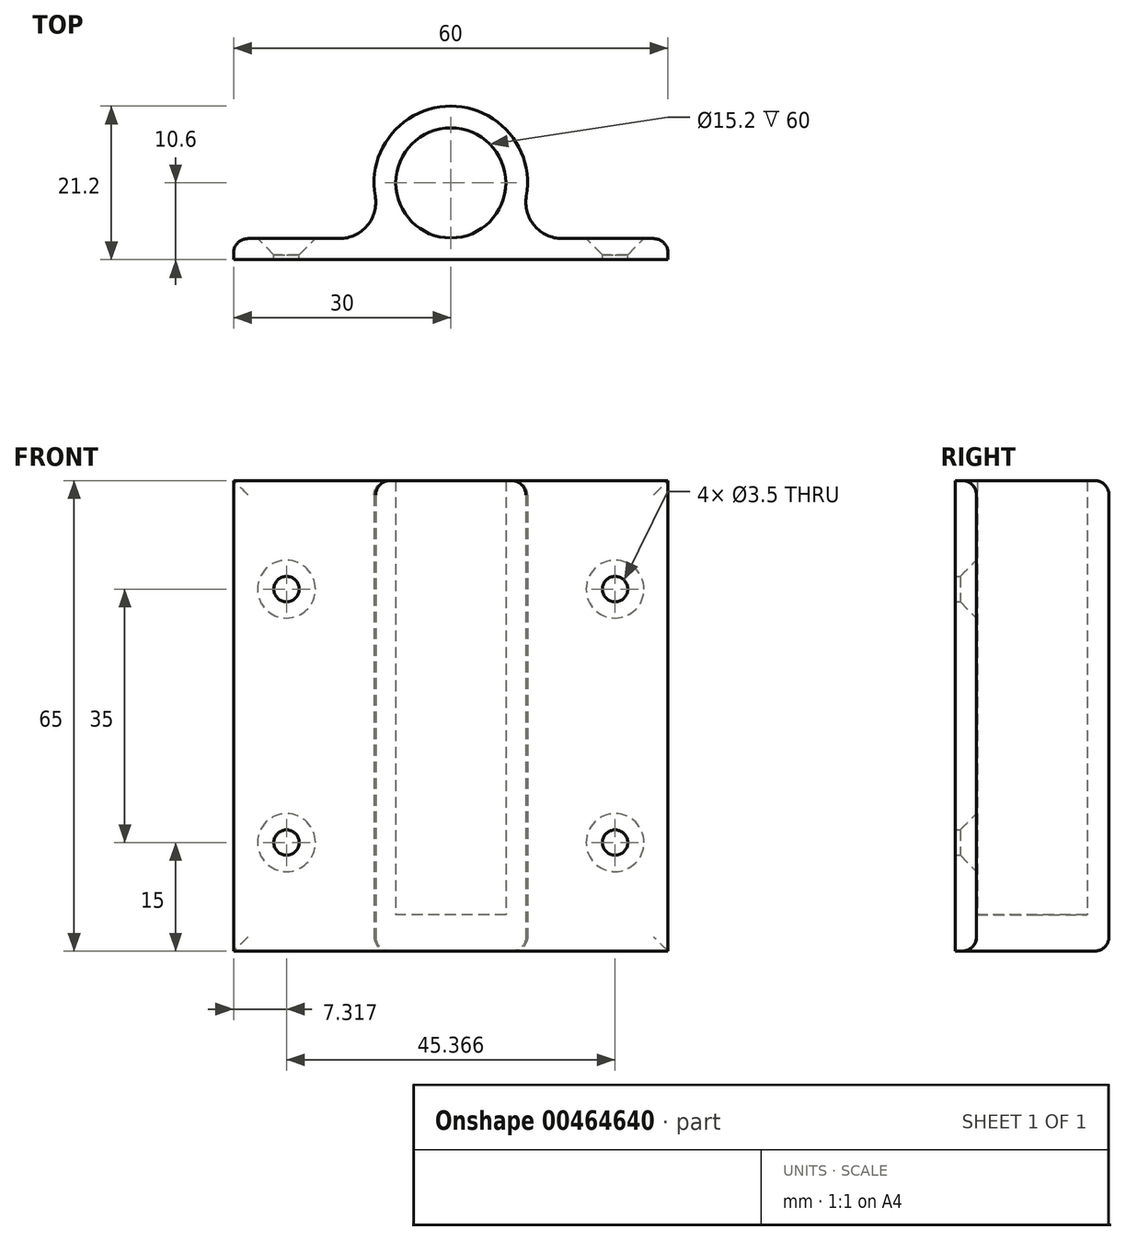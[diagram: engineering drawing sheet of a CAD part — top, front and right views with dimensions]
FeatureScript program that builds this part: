
annotation { "Feature Type Name" : "Feature", "Feature Type Description" : "" }
export const myFeature = defineFeature(function(context is Context, id is Id, definition is map)
    precondition{}
    {
        {
            var Q0;
            Q0=qCreatedBy(makeId("Top.planeOp"),FACE);
            var sketch = newSketch(context, id + "F0", { "sketchPlane" : qUnion([Q0])});
            skCircle(sketch, "E0", {"center": v(0, 0) * mm, "radius": 7.6 * mm});
            skArc(sketch, "E1.0", {"start": v(7.3, -7.7) * mm, "mid": v(0, 10.6) * mm, "end": v(-7.3, -7.7) * mm});
            skLineSegment(sketch, "E2.bottom", {"start": v(0, -10.6) * mm, "end": v(-30, -10.6) * mm});
            skLineSegment(sketch, "E2.top", {"start": v(-7.3, -7.7) * mm, "end": v(-30, -7.7) * mm});
            skLineSegment(sketch, "E2.right", {"start": v(-30, -10.6) * mm, "end": v(-30, -7.7) * mm});
            skLineSegment(sketch, "E3.bottom", {"start": v(0, -10.6) * mm, "end": v(30, -10.6) * mm});
            skLineSegment(sketch, "E3.top", {"start": v(7.3, -7.7) * mm, "end": v(30, -7.7) * mm});
            skLineSegment(sketch, "E3.right", {"start": v(30, -10.6) * mm, "end": v(30, -7.7) * mm});
            skSolve(sketch);
        }
        {
            var Q0;
            Q0=makeQuery(id+"F0.imprint","IMPRINT",FACE,{"disambiguationData":[TD([[makeQuery(id+"F0.imprint","IMPRINT",EDGE,{"derivedFrom":sQuery(id+"F0.wireOp",EDGE,"E0")}),-1.0]])]});
            var Q1;
            Q1=makeQuery(id+"F0.imprint","IMPRINT",FACE,{"disambiguationData":[TD([[makeQuery(id+"F0.imprint","IMPRINT",EDGE,{"derivedFrom":sQuery(id+"F0.wireOp",EDGE,"E0")}),1.0]])]});
            extrude(context, id + "F1", {"entities" : qUnion([Q0, Q1]), "depth" : 5 * mm});
        }
        {
            var Q0;
            Q0=makeQuery(id+"F1.opExtrude","CAP_FACE",FACE,{"disambiguationData":[OSD([sQuery(id+"F0.wireOp",EDGE,"E1.0"),sQuery(id+"F0.wireOp",EDGE,"E2.bottom"),sQuery(id+"F0.wireOp",EDGE,"E2.top"),sQuery(id+"F0.wireOp",EDGE,"E2.right"),sQuery(id+"F0.wireOp",EDGE,"E3.bottom"),sQuery(id+"F0.wireOp",EDGE,"E3.top"),sQuery(id+"F0.wireOp",EDGE,"E3.right")])],"isStart":false});
            var sketch = newSketch(context, id + "F2", { "sketchPlane" : qUnion([Q0])});
            skArc(sketch, "E4.0", {"start": v(7.3, -7.7) * mm, "mid": v(0, 10.6) * mm, "end": v(-7.3, -7.7) * mm});
            skLineSegment(sketch, "E4.1", {"start": v(7.3, -7.7) * mm, "end": v(30, -7.7) * mm});
            skLineSegment(sketch, "E4.2", {"start": v(30, -10.6) * mm, "end": v(30, -7.7) * mm});
            skLineSegment(sketch, "E4.3", {"start": v(30, -10.6) * mm, "end": v(-30, -10.6) * mm});
            skLineSegment(sketch, "E4.4", {"start": v(-30, -10.6) * mm, "end": v(-30, -7.7) * mm});
            skLineSegment(sketch, "E4.5", {"start": v(-7.3, -7.7) * mm, "end": v(-30, -7.7) * mm});
            skCircle(sketch, "E4.6", {"center": v(0, 0) * mm, "radius": 7.6 * mm});
            skSolve(sketch);
        }
        {
            var Q0;
            Q0=makeQuery(id+"F2.imprint","IMPRINT",FACE,{"disambiguationData":[TD([[makeQuery(id+"F2.imprint","IMPRINT",EDGE,{"derivedFrom":sQuery(id+"F2.wireOp",EDGE,"E4.0")}),1.0]])]});
            extrude(context, id + "F3", {"entities" : qUnion([Q0]), "operationType" : NewBodyOperationType.ADD, "depth" : 60 * mm});
        }
        {
            var Q0;
            Q0=makeQuery(id+"F3.boolean.opBoolean","MERGE",EDGE,{"derivedFrom":[makeQuery(id+"F1.opExtrude","SWEPT_EDGE",EDGE,{"disambiguationData":[OSD([sQuery(id+"F0.wireOp",EDGE,"E1.0"),sQuery(id+"F0.wireOp",EDGE,"E2.top")])]}),makeQuery(id+"F3.opExtrude","SWEPT_EDGE",EDGE,{"disambiguationData":[OSD([sQuery(id+"F2.wireOp",EDGE,"E4.0"),sQuery(id+"F2.wireOp",EDGE,"E4.5")])]})]});
            var Q1;
            Q1=makeQuery(id+"F3.boolean.opBoolean","MERGE",EDGE,{"derivedFrom":[makeQuery(id+"F1.opExtrude","SWEPT_EDGE",EDGE,{"disambiguationData":[OSD([sQuery(id+"F0.wireOp",EDGE,"E1.0"),sQuery(id+"F0.wireOp",EDGE,"E3.top")])]}),makeQuery(id+"F3.opExtrude","SWEPT_EDGE",EDGE,{"disambiguationData":[OSD([sQuery(id+"F2.wireOp",EDGE,"E4.0"),sQuery(id+"F2.wireOp",EDGE,"E4.1")])]})]});
            fillet(context, id + "F4", {"entities" : qUnion([Q0, Q1]), "radius" : 5 * mm, "tangentPropagation" : true, "allowEdgeOverflow" : false});
        }
        {
            var Q0;
            Q0=makeQuery(id+"F3.boolean.opBoolean","MERGE",FACE,{"derivedFrom":[makeQuery(id+"F1.opExtrude","SWEPT_FACE",FACE,{"disambiguationData":[OSD([sQuery(id+"F0.wireOp",EDGE,"E3.top")])]}),makeQuery(id+"F3.opExtrude","SWEPT_FACE",FACE,{"disambiguationData":[OSD([sQuery(id+"F2.wireOp",EDGE,"E4.1")])]})]});
            var sketch = newSketch(context, id + "F5", { "sketchPlane" : qUnion([Q0])});
            skLineSegment(sketch, "E5", {"start": v(-22.68, 65) * mm, "end": v(-22.68, 0) * mm, "construction": true});
            skLineSegment(sketch, "E6", {"start": v(-30, 50) * mm, "end": v(-15.37, 50) * mm, "construction": true});
            skLineSegment(sketch, "E7", {"start": v(-30, 15) * mm, "end": v(-15.37, 15) * mm, "construction": true});
            skPoint(sketch, "E8", {"position": v(-22.68, 50) * mm});
            skPoint(sketch, "E9", {"position": v(-22.68, 15) * mm});
            skLineSegment(sketch, "E10", {"start": v(0, 63) * mm, "end": v(0, 0) * mm, "construction": true});
            skPoint(sketch, "E11.MirrorP", {"position": v(22.68, 15) * mm});
            skPoint(sketch, "E12.MirrorP", {"position": v(22.68, 50) * mm});
            skSolve(sketch);
        }
        {
            var Q0;
            Q0=sQuery(id+"F5.wireOp",VERTEX,"E8");
            var Q1;
            Q1=sQuery(id+"F5.wireOp",VERTEX,"E9");
            var Q2;
            Q2=sQuery(id+"F5.wireOp",VERTEX,"E12.MirrorP");
            var Q3;
            Q3=sQuery(id+"F5.wireOp",VERTEX,"E11.MirrorP");
            var Q4;
            Q4=makeQuery(id+"F1.opExtrude","SWEPT_BODY",BODY,{"disambiguationData":[OSD([sQuery(id+"F0.wireOp",EDGE,"E1.0"),sQuery(id+"F0.wireOp",EDGE,"E2.bottom"),sQuery(id+"F0.wireOp",EDGE,"E2.top"),sQuery(id+"F0.wireOp",EDGE,"E2.right"),sQuery(id+"F0.wireOp",EDGE,"E3.bottom"),sQuery(id+"F0.wireOp",EDGE,"E3.top"),sQuery(id+"F0.wireOp",EDGE,"E3.right")])]});
            hole(context, id + "F6", {"style" : HoleStyle.C_SINK, "endStyle" : HoleEndStyle.THROUGH, "holeDiameter" : 3.5 * mm, "cSinkDiameter" : 8 * mm, "cSinkAngle" : 90 * degree, "isTappedThrough" : true, "tappedDepth" : 12 * mm, "tapClearance" : 3, "startFromSketch" : true, "locations" : qUnion([Q0, Q1, Q2, Q3]), "scope" : qUnion([Q4])});
        }
        {
            var Q0;
            Q0=makeQuery(id+"F3.opExtrude","CAP_EDGE",EDGE,{"disambiguationData":[OSD([sQuery(id+"F2.wireOp",EDGE,"E4.0")])],"isStart":false});
            var Q1;
            Q1=makeQuery(id+"F3.boolean.opBoolean","MERGE",EDGE,{"derivedFrom":[makeQuery(id+"F1.opExtrude","SWEPT_EDGE",EDGE,{"disambiguationData":[OSD([sQuery(id+"F0.wireOp",EDGE,"E2.top"),sQuery(id+"F0.wireOp",EDGE,"E2.right")])]}),makeQuery(id+"F3.opExtrude","SWEPT_EDGE",EDGE,{"disambiguationData":[OSD([sQuery(id+"F2.wireOp",EDGE,"E4.4"),sQuery(id+"F2.wireOp",EDGE,"E4.5")])]})]});
            var Q2;
            Q2=makeQuery(id+"F3.boolean.opBoolean","MERGE",EDGE,{"derivedFrom":[makeQuery(id+"F1.opExtrude","SWEPT_EDGE",EDGE,{"disambiguationData":[OSD([sQuery(id+"F0.wireOp",EDGE,"E3.top"),sQuery(id+"F0.wireOp",EDGE,"E3.right")])]}),makeQuery(id+"F3.opExtrude","SWEPT_EDGE",EDGE,{"disambiguationData":[OSD([sQuery(id+"F2.wireOp",EDGE,"E4.1"),sQuery(id+"F2.wireOp",EDGE,"E4.2")])]})]});
            var Q3;
            Q3=makeQuery(id+"F1.opExtrude","CAP_EDGE",EDGE,{"disambiguationData":[OSD([sQuery(id+"F0.wireOp",EDGE,"E3.top")])],"isStart":true});
            var Q4;
            Q4=makeQuery(id+"F1.opExtrude","CAP_EDGE",EDGE,{"disambiguationData":[OSD([sQuery(id+"F0.wireOp",EDGE,"E1.0")])],"isStart":true});
            fillet(context, id + "F7", {"entities" : qUnion([Q0, Q1, Q2, Q3, Q4]), "radius" : 2 * mm, "tangentPropagation" : true, "allowEdgeOverflow" : false});
        }
    });
